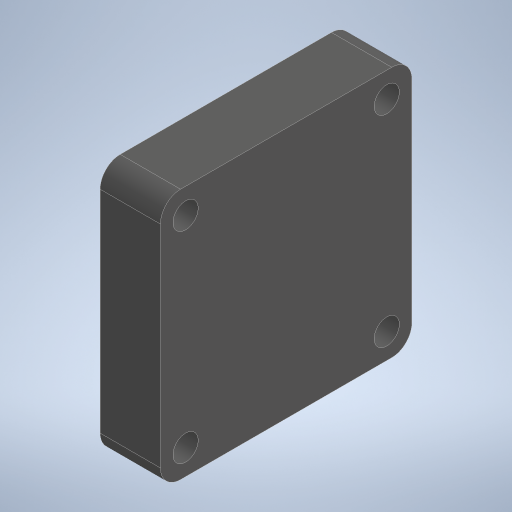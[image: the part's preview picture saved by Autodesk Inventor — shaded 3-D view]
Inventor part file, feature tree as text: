
AUTODESK INVENTOR PART (.ipt)
format: ipt  version: 2024.1 (Build 281209000, 209)  size: 224,256 bytes
history: native  units: in
note: dims shown in document units (in); Inventor stores cm internally (conversion verified against a paired STEP export)
features: extrude x2, sketch x2, fillet x1
ambient origin geometry x8: Origin, YZ Plane, XZ Plane, XY Plane, X Axis, Y Axis, Z Axis, Center Point
bodies: Solid1 (feature_tree)
feature tree (5):
  extrude  "Extrusion1"  Depth=0.9843in
  fillet  "Fillet1"  Radius=0.2362in
  extrude  "Extrusion2"  Depth=0.0787in
  sketch  "Sketch1"  dims[d0=0.9843in d1=0.9843in d2=0.2362in d3=0.0in]
  sketch  "Sketch2"  dims[d4=0.0787in d5=0.0984in d6=0.0984in d7=0.0984in d8=0.0984in d9=0.0984in d10=0.0984in d11=0.0984in d12=0.0984in d13=0.0984in d14=0.0984in d15=0.0984in d16=0.0984in d17=0.0in d18=0.0in]
